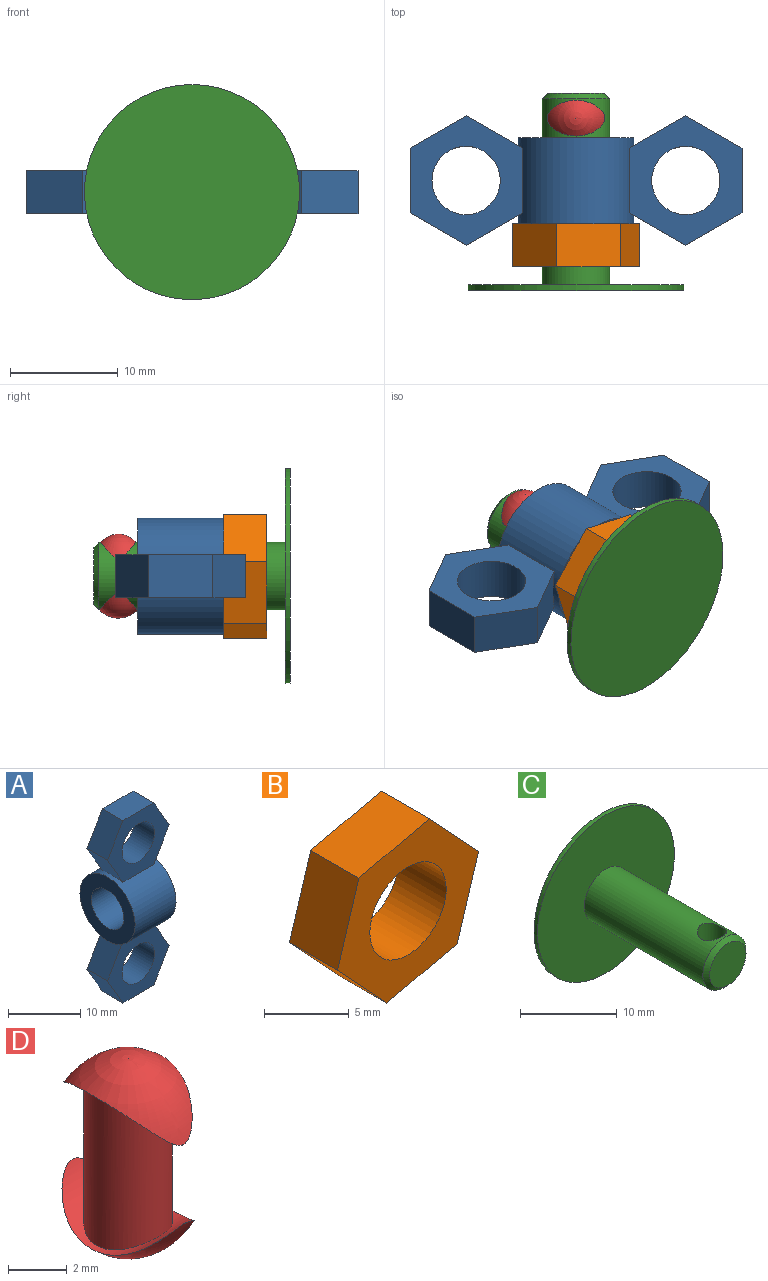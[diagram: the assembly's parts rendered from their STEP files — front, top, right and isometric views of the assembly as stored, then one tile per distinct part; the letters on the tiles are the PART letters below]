
ASSEMBLY  parts=4 mates=3
PART A: 20 faces, bbox 12x10.8x30.9 mm
  f0: plane 12.04x10.43mm, normal (0,-1,0), area 62.5mm2, adj f5,f6,f7,f8,f9,f11,f16
  f1: plane 12.04x10.43mm, normal (0,1,0), area 62.5mm2, adj f5,f6,f7,f8,f9,f11,f16
  f2: plane 6.02x4mm, normal (0,0,-1), area 24.1mm2, adj f3,f13,f14,f15
  f3: plane 5.22x4mm, normal (0.87,0,-0.5), area 24.1mm2, adj f2,f4,f14,f15
  f4: plane 5.22x4mm, normal (0.87,0,0.5), area 22.9mm2, adj f3,f14,f15,f16
  f5: plane 5.22x4mm, normal (0.87,0,-0.5), area 22.9mm2, adj f0,f1,f6,f16
  f6: plane 5.22x4mm, normal (0.87,0,0.5), area 24.1mm2, adj f0,f1,f5,f7
  f7: plane 6.02x4mm, normal (0,0,1), area 24.1mm2, adj f0,f1,f6,f8
  f8: plane 5.22x4mm, normal (-0.87,0,0.5), area 24.1mm2, adj f0,f1,f7,f9
  f9: plane 5.22x4mm, normal (-0.87,0,-0.5), area 22.9mm2, adj f0,f1,f8,f16
  f10: plane 5.22x4mm, normal (-0.87,0,0.5), area 22.9mm2, adj f13,f14,f15,f16
  f11: cylinder r=3.17mm len=6.35mm, axis (0,1,0), area 79.8mm2, adj f0,f1
  f12: cylinder r=3.17mm len=6.35mm, axis (0,1,0), area 79.8mm2, adj f14,f15
  f13: plane 5.22x4mm, normal (-0.87,0,-0.5), area 24.1mm2, adj f2,f10,f14,f15
  f14: plane 12.04x10.43mm, normal (0,-1,0), area 62.5mm2, adj f2,f3,f4,f10,f12,f13,f16
  f15: plane 12.04x10.43mm, normal (0,1,0), area 62.5mm2, adj f2,f3,f4,f10,f12,f13,f16
  f16: cylinder r=5.39mm len=10.77mm, axis (-1,0,0), area 218.9mm2, adj f0,f1,f4,f5,f9,f10,f14,f15
  f17: cylinder r=3.17mm len=8mm, axis (-1,0,0), area 159.6mm2, adj f18,f19
  f18: plane 10.77x10.77mm, normal (1,0,0), area 59.4mm2, adj f16,f17
  f19: plane 10.77x10.77mm, normal (-1,0,0), area 59.4mm2, adj f16,f17
PART B: 9 faces, bbox 11.7x4x11.5 mm
  f0: plane 5.87x4mm, normal (-0.22,0,0.97), area 24.1mm2, adj f1,f6,f7,f8
  f1: plane 5.76x4mm, normal (-0.96,0,0.29), area 24.1mm2, adj f0,f2,f7,f8
  f2: plane 4.41x4.1mm, normal (-0.73,0,-0.68), area 24.1mm2, adj f1,f3,f7,f8
  f3: plane 5.87x4mm, normal (0.22,0,-0.97), area 24.1mm2, adj f2,f4,f7,f8
  f4: plane 5.76x4mm, normal (0.96,0,-0.29), area 24.1mm2, adj f3,f6,f7,f8
  f5: cylinder r=3.17mm len=6.35mm, axis (0,1,0), area 79.8mm2, adj f7,f8
  f6: plane 4.41x4.1mm, normal (0.73,0,0.68), area 24.1mm2, adj f0,f4,f7,f8
  f7: plane 11.74x11.51mm, normal (0,-1,0), area 62.5mm2, adj f0,f1,f2,f3,f4,f5,f6
  f8: plane 11.74x11.51mm, normal (0,1,0), area 62.5mm2, adj f0,f1,f2,f3,f4,f5,f6
PART C: 7 faces, bbox 20x18.3x20 mm
  f0: cylinder r=3.15mm len=17.3mm, axis (0,1,0), area 327.8mm2, adj f4,f5,f6
  f1: plane 5.3x5.3mm, normal (0,-1,0), area 22.1mm2, adj f5
  f2: cylinder r=10mm len=20mm, axis (0,-1,0), area 31.4mm2, adj f3,f4
  f3: plane 20x20mm, normal (0,1,0), area 314.2mm2, adj f2
  f4: plane 20x20mm, normal (0,-1,0), area 283mm2, adj f0,f2
  f5: cone r=2.65mm half-angle=45deg, axis (0,1,0), area 12.9mm2, adj f0,f1
  f6: cylinder r=1.5mm len=6.3mm, axis (0,0,1), area 55.9mm2, adj f0
PART D: 5 faces, bbox 5.4x5.4x7.8 mm
  f0: cylinder r=3.15mm len=5.37mm, axis (-1,0,0), area 9.4mm2, adj f1,f2
  f1: revolved ~5.37x5.37mm, area 20.6mm2, adj f0
  f2: cylinder r=1.5mm len=6.3mm, axis (0,0,-1), area 59.4mm2, adj f0,f3
  f3: cylinder r=3.15mm len=5.37mm, axis (-1,0,0), area 7.9mm2, adj f2,f4
  f4: revolved ~5.37x5.37mm, area 18.5mm2, adj f3
PLACE A rot(axis=(0.58,0.58,0.58),120deg) t=(190.8,6.56,-172.84)mm
PLACE B rot(axis=(0,0,1),180deg) t=(180.59,-1.45,-174.84)mm
PLACE C rot(axis=(0,0,1),180deg) t=(180.59,-3.15,-174.84)mm
PLACE D rot(axis=(0,0,1),90deg) t=(180.59,12.35,-177.98)mm
MATE fastened A.f16 <-> B.f5  axis (0,-1,0) through (180.59,2.55,-174.84)mm
MATE fastened D.f2 <-> C.f6  axis (0,0,-1) through (180.59,12.35,-174.83)mm
MATE fastened B.f5 <-> C.f0  axis (0,-1,0) through (180.59,-1.45,-174.84)mm
